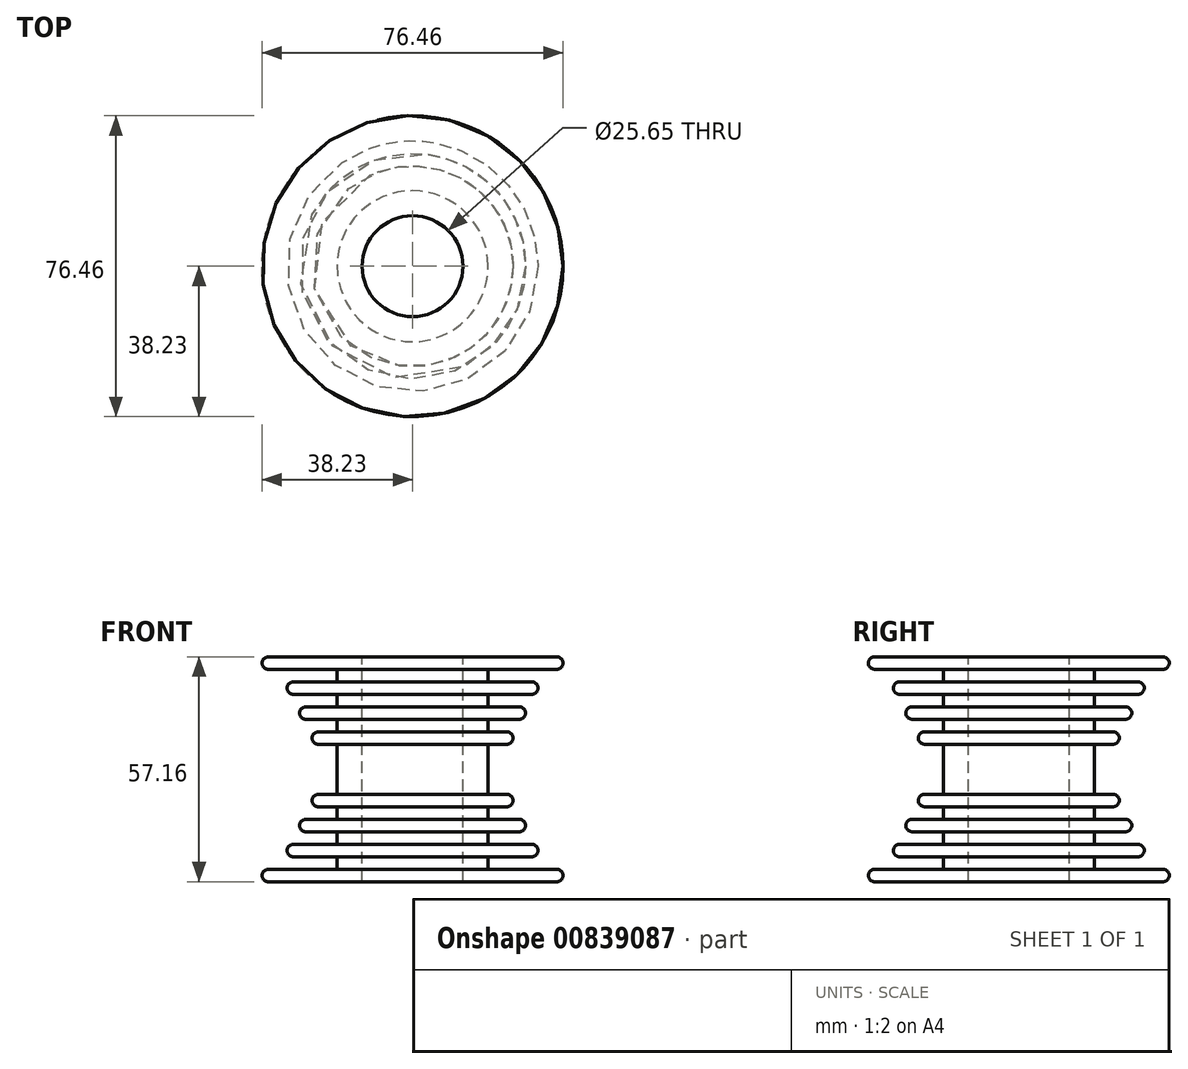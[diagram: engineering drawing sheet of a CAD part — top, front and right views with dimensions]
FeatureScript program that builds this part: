
annotation { "Feature Type Name" : "Feature", "Feature Type Description" : "" }
export const myFeature = defineFeature(function(context is Context, id is Id, definition is map)
    precondition{}
    {
        {
            var Q0;
            Q0=qCreatedBy(makeId("Front.planeOp"),FACE);
            var sketch = newSketch(context, id + "F0", { "sketchPlane" : qUnion([Q0])});
            skLineSegment(sketch, "E0", {"start": v(-12.83, -28.58) * mm, "end": v(-36.64, -28.58) * mm});
            skLineSegment(sketch, "E1", {"start": v(-38.23, -26.99) * mm, "end": v(-38.23, -26.99) * mm});
            skLineSegment(sketch, "E2", {"start": v(-36.64, -25.4) * mm, "end": v(-19.18, -25.4) * mm});
            skLineSegment(sketch, "E3", {"start": v(-19.18, -25.4) * mm, "end": v(-19.18, -22.23) * mm});
            skLineSegment(sketch, "E4", {"start": v(-19.18, -22.23) * mm, "end": v(-30.29, -22.23) * mm});
            skLineSegment(sketch, "E5", {"start": v(-31.88, -20.64) * mm, "end": v(-31.88, -20.64) * mm});
            skLineSegment(sketch, "E6", {"start": v(-30.29, -19.05) * mm, "end": v(-19.18, -19.05) * mm});
            skLineSegment(sketch, "E7", {"start": v(-19.18, -19.05) * mm, "end": v(-19.18, -15.88) * mm});
            skLineSegment(sketch, "E8", {"start": v(-19.18, -15.88) * mm, "end": v(-27.11, -15.88) * mm});
            skLineSegment(sketch, "E9", {"start": v(-28.7, -14.29) * mm, "end": v(-28.7, -14.29) * mm});
            skLineSegment(sketch, "E10", {"start": v(-27.11, -12.7) * mm, "end": v(-19.18, -12.7) * mm});
            skLineSegment(sketch, "E11", {"start": v(-19.18, -12.7) * mm, "end": v(-19.18, -9.53) * mm});
            skLineSegment(sketch, "E12", {"start": v(-19.18, -9.53) * mm, "end": v(-23.94, -9.53) * mm});
            skLineSegment(sketch, "E13", {"start": v(-25.53, -7.94) * mm, "end": v(-25.53, -7.94) * mm});
            skLineSegment(sketch, "E14", {"start": v(-23.94, -6.35) * mm, "end": v(-19.18, -6.35) * mm});
            skLineSegment(sketch, "E15", {"start": v(-19.18, -6.35) * mm, "end": v(-19.18, 0) * mm});
            skLineSegment(sketch, "E16", {"start": v(0, 0) * mm, "end": v(-6.36, 0) * mm, "construction": true});
            skLineSegment(sketch, "E17.MirrorCS", {"start": v(-19.18, 6.35) * mm, "end": v(-19.18, 0) * mm});
            skLineSegment(sketch, "E18.MirrorCS", {"start": v(-23.94, 6.35) * mm, "end": v(-19.18, 6.35) * mm});
            skLineSegment(sketch, "E19.MirrorCS", {"start": v(-25.53, 7.94) * mm, "end": v(-25.53, 7.94) * mm});
            skLineSegment(sketch, "E20.MirrorCS", {"start": v(-19.18, 9.53) * mm, "end": v(-23.94, 9.53) * mm});
            skLineSegment(sketch, "E21.MirrorCS", {"start": v(-19.18, 12.7) * mm, "end": v(-19.18, 9.53) * mm});
            skLineSegment(sketch, "E22.MirrorCS", {"start": v(-27.11, 12.7) * mm, "end": v(-19.18, 12.7) * mm});
            skLineSegment(sketch, "E23.MirrorCS", {"start": v(-28.7, 14.29) * mm, "end": v(-28.7, 14.29) * mm});
            skLineSegment(sketch, "E24.MirrorCS", {"start": v(-19.18, 15.88) * mm, "end": v(-27.11, 15.88) * mm});
            skLineSegment(sketch, "E25.MirrorCS", {"start": v(-19.18, 19.05) * mm, "end": v(-19.18, 15.88) * mm});
            skLineSegment(sketch, "E26.MirrorCS", {"start": v(-30.29, 19.05) * mm, "end": v(-19.18, 19.05) * mm});
            skLineSegment(sketch, "E27.MirrorCS", {"start": v(-19.18, 22.23) * mm, "end": v(-30.29, 22.23) * mm});
            skLineSegment(sketch, "E28.MirrorCS", {"start": v(-19.18, 25.4) * mm, "end": v(-19.18, 22.23) * mm});
            skLineSegment(sketch, "E29.MirrorCS", {"start": v(-31.88, 20.64) * mm, "end": v(-31.88, 20.64) * mm});
            skLineSegment(sketch, "E30.MirrorCS", {"start": v(-36.64, 25.4) * mm, "end": v(-19.18, 25.4) * mm});
            skLineSegment(sketch, "E31.MirrorCS", {"start": v(-38.23, 26.99) * mm, "end": v(-38.23, 26.99) * mm});
            skLineSegment(sketch, "E32.MirrorCS", {"start": v(-12.83, 28.58) * mm, "end": v(-36.64, 28.58) * mm});
            skLineSegment(sketch, "E33", {"start": v(-12.83, 28.58) * mm, "end": v(-12.83, -28.58) * mm});
            skLineSegment(sketch, "E34", {"start": v(0, 28.47) * mm, "end": v(0, -28.58) * mm, "construction": true});
            skPoint(sketch, "E35.visualSharp", {"position": v(-38.23, -28.58) * mm});
            skArc(sketch, "E35.filletArc", {"start": v(-38.23, -26.99) * mm, "mid": v(-37.76, -28.11) * mm, "end": v(-36.64, -28.58) * mm});
            skPoint(sketch, "E36.visualSharp", {"position": v(-38.23, -25.4) * mm});
            skArc(sketch, "E36.filletArc", {"start": v(-36.64, -25.4) * mm, "mid": v(-37.76, -25.86) * mm, "end": v(-38.23, -26.99) * mm});
            skPoint(sketch, "E37.visualSharp", {"position": v(-31.88, -22.23) * mm});
            skArc(sketch, "E37.filletArc", {"start": v(-31.88, -20.64) * mm, "mid": v(-31.41, -21.76) * mm, "end": v(-30.29, -22.23) * mm});
            skPoint(sketch, "E38.visualSharp", {"position": v(-31.88, -19.05) * mm});
            skArc(sketch, "E38.filletArc", {"start": v(-30.29, -19.05) * mm, "mid": v(-31.41, -19.51) * mm, "end": v(-31.88, -20.64) * mm});
            skPoint(sketch, "E39.visualSharp", {"position": v(-28.7, -15.88) * mm});
            skArc(sketch, "E39.filletArc", {"start": v(-28.7, -14.29) * mm, "mid": v(-28.24, -15.41) * mm, "end": v(-27.11, -15.88) * mm});
            skPoint(sketch, "E40.visualSharp", {"position": v(-28.7, -12.7) * mm});
            skArc(sketch, "E40.filletArc", {"start": v(-27.11, -12.7) * mm, "mid": v(-28.24, -13.16) * mm, "end": v(-28.7, -14.29) * mm});
            skPoint(sketch, "E41.visualSharp", {"position": v(-25.53, -9.53) * mm});
            skArc(sketch, "E41.filletArc", {"start": v(-25.53, -7.94) * mm, "mid": v(-25.06, -9.06) * mm, "end": v(-23.94, -9.53) * mm});
            skPoint(sketch, "E42.visualSharp", {"position": v(-25.53, -6.35) * mm});
            skArc(sketch, "E42.filletArc", {"start": v(-23.94, -6.35) * mm, "mid": v(-25.06, -6.81) * mm, "end": v(-25.53, -7.94) * mm});
            skPoint(sketch, "E43.visualSharp", {"position": v(-25.53, 6.35) * mm});
            skArc(sketch, "E43.filletArc", {"start": v(-25.53, 7.94) * mm, "mid": v(-25.06, 6.81) * mm, "end": v(-23.94, 6.35) * mm});
            skPoint(sketch, "E44.visualSharp", {"position": v(-25.53, 9.53) * mm});
            skArc(sketch, "E44.filletArc", {"start": v(-23.94, 9.53) * mm, "mid": v(-25.06, 9.06) * mm, "end": v(-25.53, 7.94) * mm});
            skPoint(sketch, "E45.visualSharp", {"position": v(-28.7, 12.7) * mm});
            skArc(sketch, "E45.filletArc", {"start": v(-28.7, 14.29) * mm, "mid": v(-28.24, 13.16) * mm, "end": v(-27.11, 12.7) * mm});
            skPoint(sketch, "E46.visualSharp", {"position": v(-28.7, 15.88) * mm});
            skArc(sketch, "E46.filletArc", {"start": v(-27.11, 15.88) * mm, "mid": v(-28.24, 15.41) * mm, "end": v(-28.7, 14.29) * mm});
            skPoint(sketch, "E47.visualSharp", {"position": v(-31.88, 19.05) * mm});
            skArc(sketch, "E47.filletArc", {"start": v(-31.88, 20.64) * mm, "mid": v(-31.41, 19.51) * mm, "end": v(-30.29, 19.05) * mm});
            skPoint(sketch, "E48.visualSharp", {"position": v(-31.88, 22.23) * mm});
            skArc(sketch, "E48.filletArc", {"start": v(-30.29, 22.23) * mm, "mid": v(-31.41, 21.76) * mm, "end": v(-31.88, 20.64) * mm});
            skPoint(sketch, "E49.visualSharp", {"position": v(-38.23, 25.4) * mm});
            skArc(sketch, "E49.filletArc", {"start": v(-38.23, 26.99) * mm, "mid": v(-37.76, 25.86) * mm, "end": v(-36.64, 25.4) * mm});
            skPoint(sketch, "E50.visualSharp", {"position": v(-38.23, 28.58) * mm});
            skArc(sketch, "E50.filletArc", {"start": v(-36.64, 28.58) * mm, "mid": v(-37.76, 28.11) * mm, "end": v(-38.23, 26.99) * mm});
            skSolve(sketch);
        }
        {
            var Q0;
            Q0=makeQuery(id+"F0.imprint","IMPRINT",FACE,{"disambiguationData":[TD([[makeQuery(id+"F0.imprint","IMPRINT",EDGE,{"derivedFrom":sQuery(id+"F0.wireOp",EDGE,"E0")}),-1.0]])]});
            var Q1;
            Q1=sQuery(id+"F0.wireOp",EDGE,"E34");
            revolve(context, id + "F1", {"surfaceOperationType" : NewSurfaceOperationType.NEW, "entities" : qUnion([Q0]), "axis" : qUnion([Q1]), "revolveType" : RevolveType.FULL});
        }
    });
